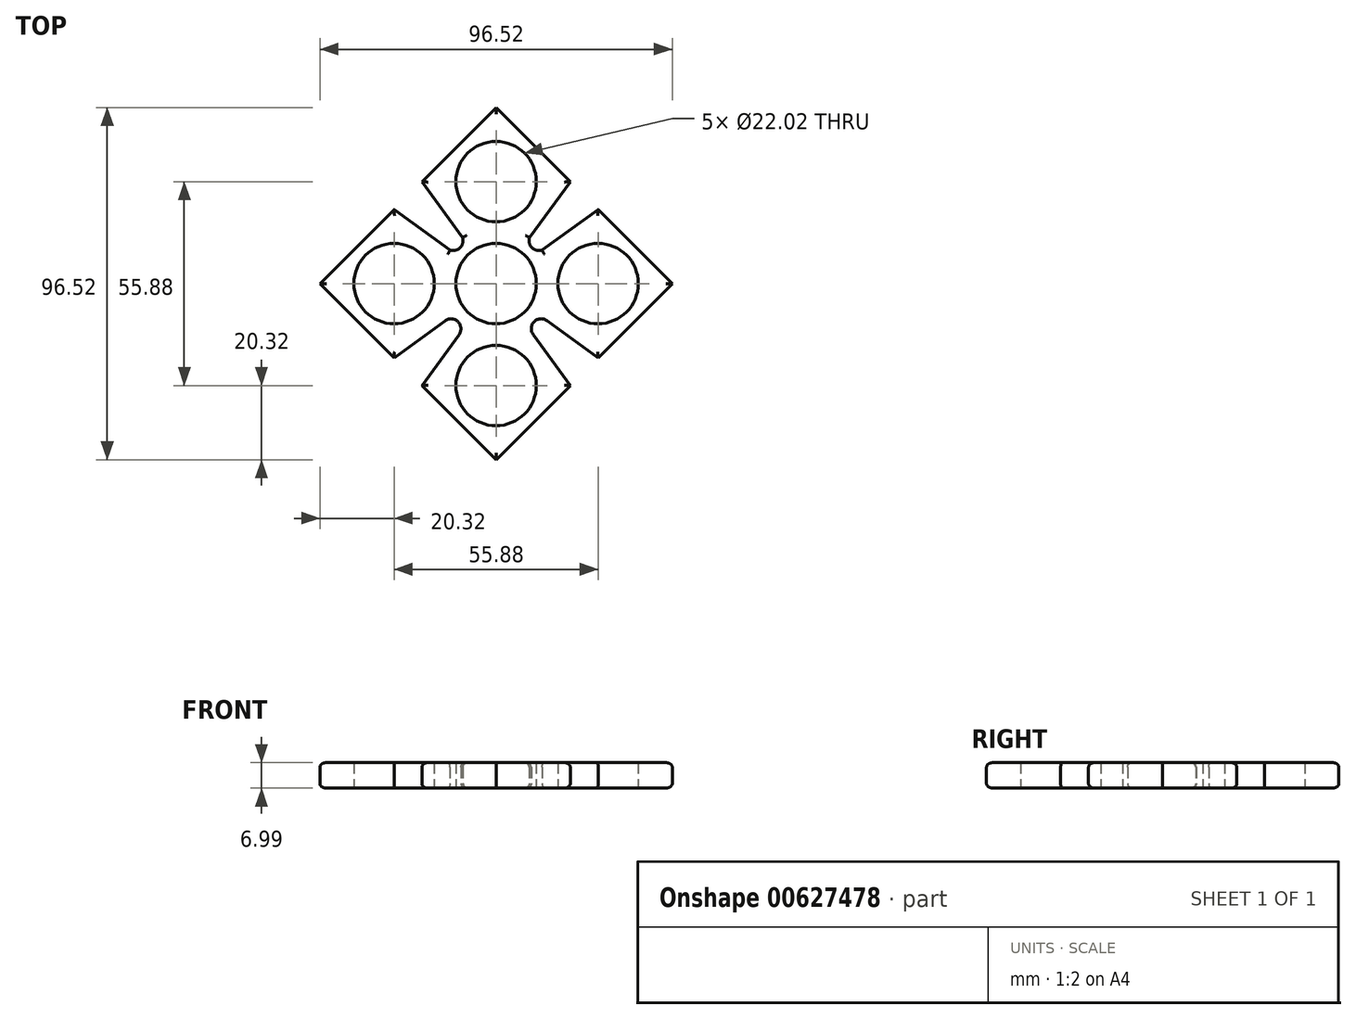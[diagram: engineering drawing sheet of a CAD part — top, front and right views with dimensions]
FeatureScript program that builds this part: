
annotation { "Feature Type Name" : "Feature", "Feature Type Description" : "" }
export const myFeature = defineFeature(function(context is Context, id is Id, definition is map)
    precondition{}
    {
        {
            var Q0;
            Q0=qCreatedBy(makeId("Top.planeOp"),FACE);
            var sketch = newSketch(context, id + "F0", { "sketchPlane" : qUnion([Q0])});
            skCircle(sketch, "E0", {"center": v(0, 0) * mm, "radius": 11.01 * mm});
            skCircle(sketch, "E1", {"center": v(0, 27.94) * mm, "radius": 11.01 * mm});
            skCircle(sketch, "E2", {"center": v(27.94, 0) * mm, "radius": 11.01 * mm});
            skCircle(sketch, "E3", {"center": v(-27.94, 0) * mm, "radius": 11.01 * mm});
            skCircle(sketch, "E4", {"center": v(0, -27.94) * mm, "radius": 11.01 * mm});
            skLineSegment(sketch, "E5", {"start": v(0, 27.94) * mm, "end": v(0, 0) * mm});
            skLineSegment(sketch, "E6", {"start": v(27.94, 0) * mm, "end": v(0, 0) * mm});
            skLineSegment(sketch, "E7", {"start": v(0, -27.94) * mm, "end": v(0, 0) * mm});
            skLineSegment(sketch, "E8", {"start": v(0, 0) * mm, "end": v(-27.94, 0) * mm});
            skLineSegment(sketch, "E9", {"start": v(-27.94, 0) * mm, "end": v(-27.94, 20.32) * mm});
            skLineSegment(sketch, "E10", {"start": v(-27.94, 0) * mm, "end": v(-27.94, -20.32) * mm});
            skLineSegment(sketch, "E11", {"start": v(-27.94, -20.32) * mm, "end": v(-48.26, 0) * mm});
            skLineSegment(sketch, "E12", {"start": v(-48.26, 0) * mm, "end": v(-27.94, 20.32) * mm});
            skLineSegment(sketch, "E13", {"start": v(0, 27.94) * mm, "end": v(-20.32, 27.94) * mm});
            skLineSegment(sketch, "E14", {"start": v(0, 27.94) * mm, "end": v(20.32, 27.94) * mm});
            skLineSegment(sketch, "E15", {"start": v(-20.32, 27.94) * mm, "end": v(0, 48.26) * mm});
            skLineSegment(sketch, "E16", {"start": v(0, 48.26) * mm, "end": v(20.32, 27.94) * mm});
            skLineSegment(sketch, "E17", {"start": v(27.94, 0) * mm, "end": v(27.94, 20.32) * mm});
            skLineSegment(sketch, "E18", {"start": v(27.94, 0) * mm, "end": v(27.94, -20.32) * mm});
            skLineSegment(sketch, "E19", {"start": v(27.94, 20.32) * mm, "end": v(48.26, 0) * mm});
            skLineSegment(sketch, "E20", {"start": v(27.94, -20.32) * mm, "end": v(48.26, 0) * mm});
            skLineSegment(sketch, "E21", {"start": v(0, -27.94) * mm, "end": v(-20.32, -27.94) * mm});
            skLineSegment(sketch, "E22", {"start": v(0, -27.94) * mm, "end": v(20.32, -27.94) * mm});
            skLineSegment(sketch, "E23", {"start": v(-20.32, -27.94) * mm, "end": v(0, -48.26) * mm});
            skLineSegment(sketch, "E24", {"start": v(20.32, -27.94) * mm, "end": v(0, -48.26) * mm});
            skLineSegment(sketch, "E25", {"start": v(-27.94, 20.32) * mm, "end": v(0, 0) * mm});
            skLineSegment(sketch, "E26", {"start": v(-20.32, 27.94) * mm, "end": v(0, 0) * mm});
            skLineSegment(sketch, "E27", {"start": v(20.32, 27.94) * mm, "end": v(0, 0) * mm});
            skLineSegment(sketch, "E28", {"start": v(27.94, 20.32) * mm, "end": v(0, 0) * mm});
            skLineSegment(sketch, "E29", {"start": v(-27.94, -20.32) * mm, "end": v(0, 0) * mm});
            skLineSegment(sketch, "E30", {"start": v(-20.32, -27.94) * mm, "end": v(0, 0) * mm});
            skLineSegment(sketch, "E31", {"start": v(27.94, -20.32) * mm, "end": v(0, 0) * mm});
            skLineSegment(sketch, "E32", {"start": v(20.32, -27.94) * mm, "end": v(0, 0) * mm});
            skLineSegment(sketch, "E33", {"start": v(-27.94, 0) * mm, "end": v(-48.26, 0) * mm});
            skLineSegment(sketch, "E34", {"start": v(27.94, 0) * mm, "end": v(48.26, 0) * mm});
            skLineSegment(sketch, "E35", {"start": v(0, 27.94) * mm, "end": v(0, 48.26) * mm});
            skLineSegment(sketch, "E36", {"start": v(0, -27.94) * mm, "end": v(0, -48.26) * mm});
            skArc(sketch, "E37", {"start": v(-10.16, -13.97) * mm, "mid": v(-10.44, -10.44) * mm, "end": v(-13.97, -10.16) * mm});
            skArc(sketch, "E38", {"start": v(13.97, -10.16) * mm, "mid": v(10.44, -10.44) * mm, "end": v(10.16, -13.97) * mm});
            skPoint(sketch, "E38.midSnap0", {"position": v(13.97, -10.16) * mm});
            skPoint(sketch, "E38.midSnap1", {"position": v(10.16, -13.97) * mm});
            skArc(sketch, "E39", {"start": v(10.16, 13.97) * mm, "mid": v(9.84, 9.84) * mm, "end": v(13.97, 10.16) * mm});
            skPoint(sketch, "E39.midSnap0", {"position": v(10.16, 13.97) * mm});
            skPoint(sketch, "E39.midSnap1", {"position": v(13.97, 10.16) * mm});
            skArc(sketch, "E40", {"start": v(-13.97, 10.16) * mm, "mid": v(-9.84, 9.84) * mm, "end": v(-10.16, 13.97) * mm});
            skPoint(sketch, "E40.midSnap0", {"position": v(-13.97, 10.16) * mm});
            skPoint(sketch, "E40.midSnap1", {"position": v(-10.16, 13.97) * mm});
            skSolve(sketch);
        }
        {
            var Q0;
            Q0 = qSketchRegion(id + "F0", true);
            extrude(context, id + "F1", {"entities" : qUnion([Q0]), "depth" : 7 * mm, "offsetDistance" : 25.4 * mm});
        }
        {
            var Q0;
            Q0=makeQuery(id+"F1.opExtrude","CAP_EDGE",EDGE,{"disambiguationData":[OSD([sQuery(id+"F0.wireOp",EDGE,"E12")])],"isStart":false});
            var Q1;
            Q1=makeQuery(id+"F1.opExtrude","CAP_EDGE",EDGE,{"disambiguationData":[OSD([sQuery(id+"F0.wireOp",EDGE,"E25")])],"isStart":false});
            var Q2;
            Q2=makeQuery(id+"F1.opExtrude","CAP_EDGE",EDGE,{"disambiguationData":[OSD([sQuery(id+"F0.wireOp",EDGE,"E26")])],"isStart":false});
            var Q3;
            Q3=makeQuery(id+"F1.opExtrude","CAP_EDGE",EDGE,{"disambiguationData":[OSD([sQuery(id+"F0.wireOp",EDGE,"E15")])],"isStart":false});
            var Q4;
            Q4=makeQuery(id+"F1.opExtrude","CAP_EDGE",EDGE,{"disambiguationData":[OSD([sQuery(id+"F0.wireOp",EDGE,"E16")])],"isStart":false});
            var Q5;
            Q5=makeQuery(id+"F1.opExtrude","CAP_EDGE",EDGE,{"disambiguationData":[OSD([sQuery(id+"F0.wireOp",EDGE,"E27")])],"isStart":false});
            var Q6;
            Q6=makeQuery(id+"F1.opExtrude","CAP_EDGE",EDGE,{"disambiguationData":[OSD([sQuery(id+"F0.wireOp",EDGE,"E28")])],"isStart":false});
            var Q7;
            Q7=makeQuery(id+"F1.opExtrude","CAP_EDGE",EDGE,{"disambiguationData":[OSD([sQuery(id+"F0.wireOp",EDGE,"E31")])],"isStart":false});
            var Q8;
            Q8=makeQuery(id+"F1.opExtrude","CAP_EDGE",EDGE,{"disambiguationData":[OSD([sQuery(id+"F0.wireOp",EDGE,"E32")])],"isStart":false});
            var Q9;
            Q9=makeQuery(id+"F1.opExtrude","CAP_EDGE",EDGE,{"disambiguationData":[OSD([sQuery(id+"F0.wireOp",EDGE,"E19")])],"isStart":false});
            var Q10;
            Q10=makeQuery(id+"F1.opExtrude","CAP_EDGE",EDGE,{"disambiguationData":[OSD([sQuery(id+"F0.wireOp",EDGE,"E20")])],"isStart":false});
            var Q11;
            Q11=makeQuery(id+"F1.opExtrude","CAP_EDGE",EDGE,{"disambiguationData":[OSD([sQuery(id+"F0.wireOp",EDGE,"E24")])],"isStart":false});
            var Q12;
            Q12=makeQuery(id+"F1.opExtrude","CAP_EDGE",EDGE,{"disambiguationData":[OSD([sQuery(id+"F0.wireOp",EDGE,"E23")])],"isStart":false});
            var Q13;
            Q13=makeQuery(id+"F1.opExtrude","CAP_EDGE",EDGE,{"disambiguationData":[OSD([sQuery(id+"F0.wireOp",EDGE,"E30")])],"isStart":false});
            var Q14;
            Q14=makeQuery(id+"F1.opExtrude","CAP_EDGE",EDGE,{"disambiguationData":[OSD([sQuery(id+"F0.wireOp",EDGE,"E29")])],"isStart":false});
            var Q15;
            Q15=makeQuery(id+"F1.opExtrude","CAP_EDGE",EDGE,{"disambiguationData":[OSD([sQuery(id+"F0.wireOp",EDGE,"E11")])],"isStart":false});
            var Q16;
            Q16=makeQuery(id+"F1.opExtrude","CAP_EDGE",EDGE,{"disambiguationData":[OSD([sQuery(id+"F0.wireOp",EDGE,"E37")])],"isStart":false});
            var Q17;
            Q17=makeQuery(id+"F1.opExtrude","CAP_EDGE",EDGE,{"disambiguationData":[OSD([sQuery(id+"F0.wireOp",EDGE,"E40")])],"isStart":false});
            var Q18;
            Q18=makeQuery(id+"F1.opExtrude","CAP_EDGE",EDGE,{"disambiguationData":[OSD([sQuery(id+"F0.wireOp",EDGE,"E39")])],"isStart":false});
            var Q19;
            Q19=makeQuery(id+"F1.opExtrude","CAP_EDGE",EDGE,{"disambiguationData":[OSD([sQuery(id+"F0.wireOp",EDGE,"E38")])],"isStart":false});
            fillet(context, id + "F2", {"entities" : qUnion([Q0, Q1, Q2, Q3, Q4, Q5, Q6, Q7, Q8, Q9, Q10, Q11, Q12, Q13, Q14, Q15, Q16, Q17, Q18, Q19]), "radius" : 1.27 * mm, "tangentPropagation" : true, "allowEdgeOverflow" : false});
        }
        {
            var Q0;
            Q0=makeQuery(id+"F1.opExtrude","CAP_EDGE",EDGE,{"disambiguationData":[OSD([sQuery(id+"F0.wireOp",EDGE,"E23")])],"isStart":true});
            var Q1;
            Q1=makeQuery(id+"F1.opExtrude","CAP_EDGE",EDGE,{"disambiguationData":[OSD([sQuery(id+"F0.wireOp",EDGE,"E24")])],"isStart":true});
            var Q2;
            Q2=makeQuery(id+"F1.opExtrude","CAP_EDGE",EDGE,{"disambiguationData":[OSD([sQuery(id+"F0.wireOp",EDGE,"E32")])],"isStart":true});
            var Q3;
            Q3=makeQuery(id+"F1.opExtrude","CAP_EDGE",EDGE,{"disambiguationData":[OSD([sQuery(id+"F0.wireOp",EDGE,"E31")])],"isStart":true});
            var Q4;
            Q4=makeQuery(id+"F1.opExtrude","CAP_EDGE",EDGE,{"disambiguationData":[OSD([sQuery(id+"F0.wireOp",EDGE,"E20")])],"isStart":true});
            var Q5;
            Q5=makeQuery(id+"F1.opExtrude","CAP_EDGE",EDGE,{"disambiguationData":[OSD([sQuery(id+"F0.wireOp",EDGE,"E19")])],"isStart":true});
            var Q6;
            Q6=makeQuery(id+"F1.opExtrude","CAP_EDGE",EDGE,{"disambiguationData":[OSD([sQuery(id+"F0.wireOp",EDGE,"E16")])],"isStart":true});
            var Q7;
            Q7=makeQuery(id+"F1.opExtrude","CAP_EDGE",EDGE,{"disambiguationData":[OSD([sQuery(id+"F0.wireOp",EDGE,"E27")])],"isStart":true});
            var Q8;
            Q8=makeQuery(id+"F1.opExtrude","CAP_EDGE",EDGE,{"disambiguationData":[OSD([sQuery(id+"F0.wireOp",EDGE,"E28")])],"isStart":true});
            var Q9;
            Q9=makeQuery(id+"F1.opExtrude","CAP_EDGE",EDGE,{"disambiguationData":[OSD([sQuery(id+"F0.wireOp",EDGE,"E39")])],"isStart":true});
            var Q10;
            Q10=makeQuery(id+"F1.opExtrude","CAP_EDGE",EDGE,{"disambiguationData":[OSD([sQuery(id+"F0.wireOp",EDGE,"E40")])],"isStart":true});
            var Q11;
            Q11=makeQuery(id+"F1.opExtrude","CAP_EDGE",EDGE,{"disambiguationData":[OSD([sQuery(id+"F0.wireOp",EDGE,"E26")])],"isStart":true});
            var Q12;
            Q12=makeQuery(id+"F1.opExtrude","CAP_EDGE",EDGE,{"disambiguationData":[OSD([sQuery(id+"F0.wireOp",EDGE,"E15")])],"isStart":true});
            var Q13;
            Q13=makeQuery(id+"F1.opExtrude","CAP_EDGE",EDGE,{"disambiguationData":[OSD([sQuery(id+"F0.wireOp",EDGE,"E12")])],"isStart":true});
            var Q14;
            Q14=makeQuery(id+"F1.opExtrude","CAP_EDGE",EDGE,{"disambiguationData":[OSD([sQuery(id+"F0.wireOp",EDGE,"E25")])],"isStart":true});
            var Q15;
            Q15=makeQuery(id+"F1.opExtrude","CAP_EDGE",EDGE,{"disambiguationData":[OSD([sQuery(id+"F0.wireOp",EDGE,"E11")])],"isStart":true});
            var Q16;
            Q16=makeQuery(id+"F1.opExtrude","CAP_EDGE",EDGE,{"disambiguationData":[OSD([sQuery(id+"F0.wireOp",EDGE,"E30")])],"isStart":true});
            var Q17;
            Q17=makeQuery(id+"F1.opExtrude","CAP_EDGE",EDGE,{"disambiguationData":[OSD([sQuery(id+"F0.wireOp",EDGE,"E37")])],"isStart":true});
            var Q18;
            Q18=makeQuery(id+"F1.opExtrude","CAP_EDGE",EDGE,{"disambiguationData":[OSD([sQuery(id+"F0.wireOp",EDGE,"E29")])],"isStart":true});
            fillet(context, id + "F3", {"entities" : qUnion([Q0, Q1, Q2, Q3, Q4, Q5, Q6, Q7, Q8, Q9, Q10, Q11, Q12, Q13, Q14, Q15, Q16, Q17, Q18]), "radius" : 1.27 * mm, "tangentPropagation" : true, "allowEdgeOverflow" : false});
        }
    });
